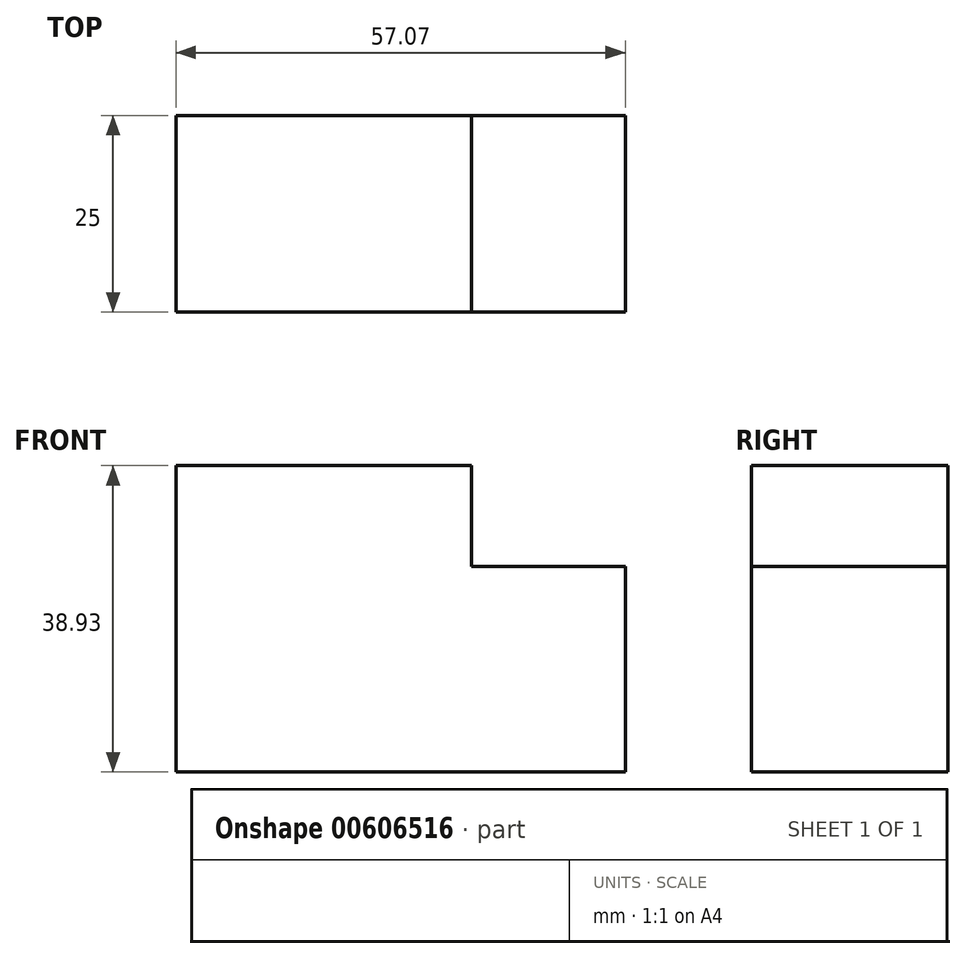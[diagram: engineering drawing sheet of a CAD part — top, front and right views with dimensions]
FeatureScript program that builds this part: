
annotation { "Feature Type Name" : "Feature", "Feature Type Description" : "" }
export const myFeature = defineFeature(function(context is Context, id is Id, definition is map)
    precondition{}
    {
        {
            var Q0;
            Q0=qCreatedBy(makeId("Front.planeOp"),FACE);
            var sketch = newSketch(context, id + "F0", { "sketchPlane" : qUnion([Q0])});
            skLineSegment(sketch, "E0", {"start": v(-39.85, 26.48) * mm, "end": v(-39.85, -12.45) * mm});
            skLineSegment(sketch, "E1", {"start": v(-39.85, -12.45) * mm, "end": v(17.22, -12.45) * mm});
            skLineSegment(sketch, "E2", {"start": v(17.22, -12.45) * mm, "end": v(17.22, 13.65) * mm});
            skLineSegment(sketch, "E3", {"start": v(17.22, 13.65) * mm, "end": v(-2.35, 13.65) * mm});
            skLineSegment(sketch, "E4", {"start": v(-2.35, 13.65) * mm, "end": v(-2.35, 26.77) * mm});
            skLineSegment(sketch, "E5", {"start": v(-39.85, 26.48) * mm, "end": v(-2.35, 26.48) * mm});
            skSolve(sketch);
        }
        {
            var Q0;
            Q0=makeQuery(id+"F0.imprint","IMPRINT",FACE,{"disambiguationData":[TD([[makeQuery(id+"F0.imprint","IMPRINT",EDGE,{"derivedFrom":sQuery(id+"F0.wireOp",EDGE,"E0")}),1.0]])]});
            extrude(context, id + "F1", {"entities" : qUnion([Q0]), "depth" : 25 * mm, "offsetDistance" : 25 * mm});
        }
    });
